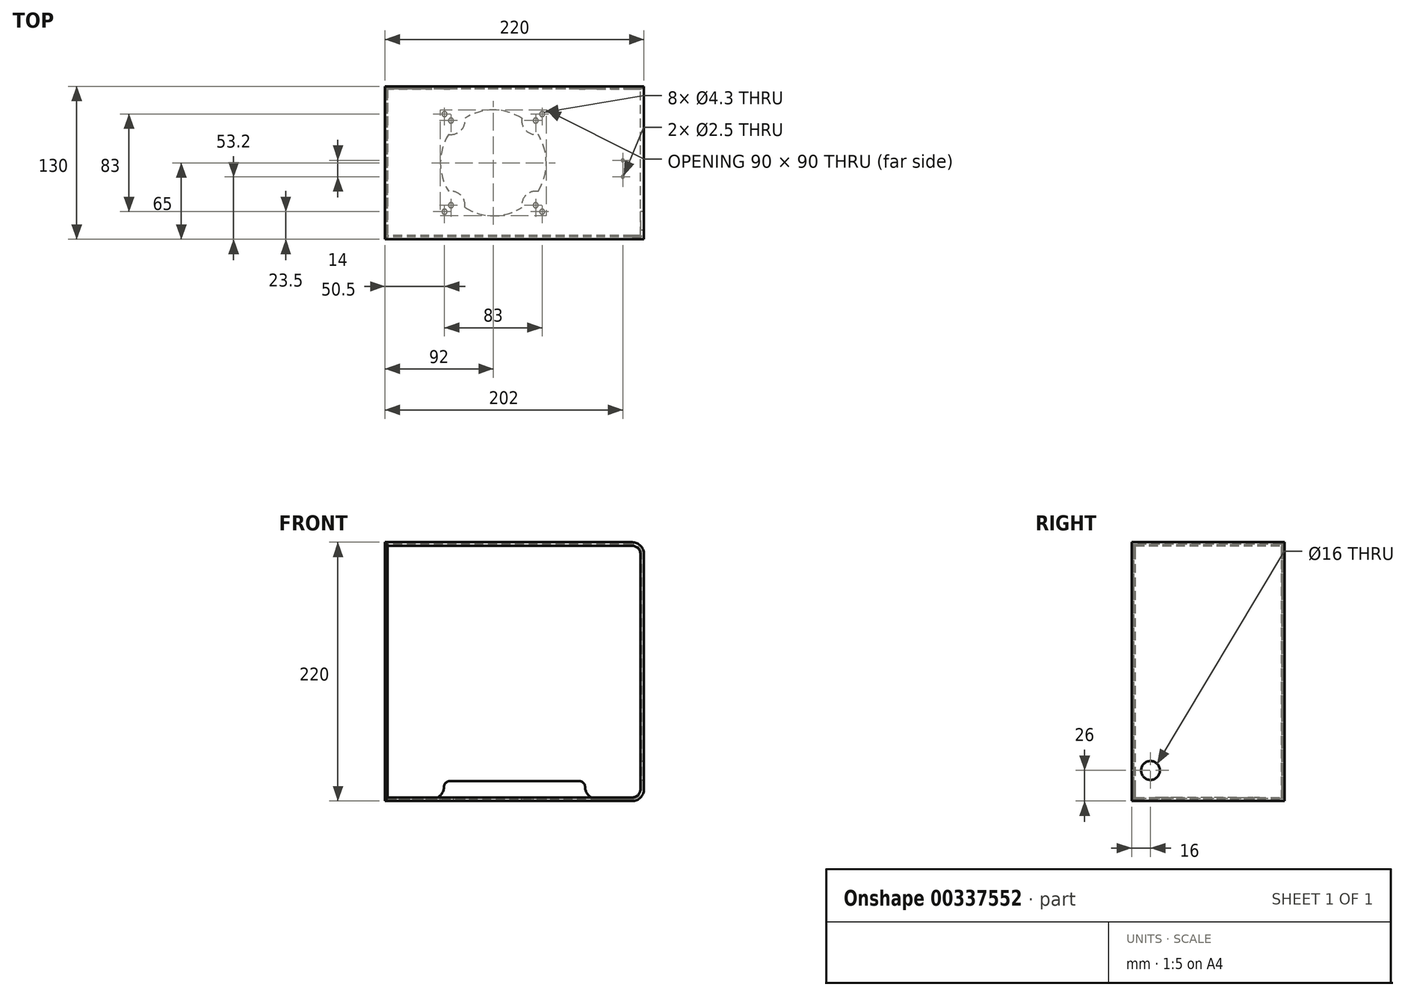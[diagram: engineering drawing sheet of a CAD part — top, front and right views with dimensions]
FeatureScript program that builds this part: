
annotation { "Feature Type Name" : "Feature", "Feature Type Description" : "" }
export const myFeature = defineFeature(function(context is Context, id is Id, definition is map)
    precondition{}
    {
        {
            var Q0;
            Q0=qCreatedBy(makeId("Right.planeOp"),FACE);
            var sketch = newSketch(context, id + "F0", { "sketchPlane" : qUnion([Q0])});
            skLineSegment(sketch, "E0.bottom", {"start": v(-65, 0) * mm, "end": v(65, 0) * mm});
            skLineSegment(sketch, "E0.top", {"start": v(-65, 3) * mm, "end": v(-63, 3) * mm});
            skLineSegment(sketch, "E0.left", {"start": v(-65, 0) * mm, "end": v(-65, 3) * mm});
            skLineSegment(sketch, "E0.right", {"start": v(65, 0) * mm, "end": v(65, 3) * mm});
            skLineSegment(sketch, "E1.top", {"start": v(-63, 1.9) * mm, "end": v(-61.8, 1.9) * mm});
            skLineSegment(sketch, "E1.left", {"start": v(-63, 3) * mm, "end": v(-63, 1.9) * mm});
            skLineSegment(sketch, "E1.right", {"start": v(-61.8, 3) * mm, "end": v(-61.8, 1.9) * mm});
            skLineSegment(sketch, "E2.trimOffspring", {"start": v(-61.8, 3) * mm, "end": v(62.8, 3) * mm});
            skLineSegment(sketch, "E3.top", {"start": v(64, 1.9) * mm, "end": v(62.8, 1.9) * mm});
            skLineSegment(sketch, "E3.left", {"start": v(64, 3) * mm, "end": v(64, 1.9) * mm});
            skLineSegment(sketch, "E3.right", {"start": v(62.8, 3) * mm, "end": v(62.8, 1.9) * mm});
            skLineSegment(sketch, "E4.trimOffspring", {"start": v(64, 3) * mm, "end": v(65, 3) * mm});
            skSolve(sketch);
        }
        {
            var Q0;
            Q0=qCreatedBy(makeId("Front.planeOp"),FACE);
            var sketch = newSketch(context, id + "F1", { "sketchPlane" : qUnion([Q0])});
            skLineSegment(sketch, "E5", {"start": v(0, 0) * mm, "end": v(210, 0) * mm});
            skLineSegment(sketch, "E6", {"start": v(220, 10) * mm, "end": v(220, 210) * mm});
            skLineSegment(sketch, "E7", {"start": v(210, 220) * mm, "end": v(0, 220) * mm});
            skPoint(sketch, "E8.visualSharp", {"position": v(220, 220) * mm});
            skArc(sketch, "E8.filletArc", {"start": v(220, 210) * mm, "mid": v(217.07, 217.07) * mm, "end": v(210, 220) * mm});
            skPoint(sketch, "E9.visualSharp", {"position": v(220, 0) * mm});
            skArc(sketch, "E9.filletArc", {"start": v(210, 0) * mm, "mid": v(217.07, 2.93) * mm, "end": v(220, 10) * mm});
            skSolve(sketch);
        }
        {
            var Q0;
            Q0=makeQuery(id+"F0.imprint","IMPRINT",FACE,{"disambiguationData":[TD([[makeQuery(id+"F0.imprint","IMPRINT",EDGE,{"derivedFrom":sQuery(id+"F0.wireOp",EDGE,"E0.bottom")}),1.0]])]});
            var Q1;
            Q1=qConstructionFilter(qBodyType(qCreatedBy(id+"F1",EDGE),BodyType.WIRE),ConstructionObject.NO);
            sweep(context, id + "F2", {"profiles" : qUnion([Q0]), "path" : qUnion([Q1])});
        }
        {
            var Q0;
            Q0=makeQuery(id+"F2.opSweep","SWEPT_FACE",FACE,{"disambiguationData":[OSD([sQuery(id+"F0.wireOp",EDGE,"E2.trimOffspring"),sQuery(id+"F1.wireOp",EDGE,"E5")])]});
            var sketch = newSketch(context, id + "F3", { "sketchPlane" : qUnion([Q0])});
            skLineSegment(sketch, "E10.bottom", {"start": v(56, 36) * mm, "end": v(128, 36) * mm, "construction": true});
            skLineSegment(sketch, "E10.top", {"start": v(56, -36) * mm, "end": v(128, -36) * mm, "construction": true});
            skLineSegment(sketch, "E10.left", {"start": v(56, 36) * mm, "end": v(56, -36) * mm, "construction": true});
            skLineSegment(sketch, "E10.right", {"start": v(128, 36) * mm, "end": v(128, -36) * mm, "construction": true});
            skLineSegment(sketch, "E11.bottom", {"start": v(50.5, 41.5) * mm, "end": v(133.5, 41.5) * mm, "construction": true});
            skLineSegment(sketch, "E11.top", {"start": v(50.5, -41.5) * mm, "end": v(133.5, -41.5) * mm, "construction": true});
            skLineSegment(sketch, "E11.left", {"start": v(50.5, 41.5) * mm, "end": v(50.5, -41.5) * mm, "construction": true});
            skLineSegment(sketch, "E11.right", {"start": v(133.5, 41.5) * mm, "end": v(133.5, -41.5) * mm, "construction": true});
            skLineSegment(sketch, "E12", {"start": v(50.5, 41.5) * mm, "end": v(56, 36) * mm, "construction": true});
            skLineSegment(sketch, "E13", {"start": v(128, -36) * mm, "end": v(133.5, -41.5) * mm, "construction": true});
            skArc(sketch, "E14", {"start": v(54.09, 24.24) * mm, "mid": v(47.72, -8.02) * mm, "end": v(65, -36) * mm});
            skLineSegment(sketch, "E15", {"start": v(56, 36) * mm, "end": v(92, 0) * mm, "construction": true});
            skLineSegment(sketch, "E16", {"start": v(92, 0) * mm, "end": v(128, -36) * mm, "construction": true});
            skCircle(sketch, "E17", {"center": v(56, 36) * mm, "radius": 2.15 * mm});
            skCircle(sketch, "E18", {"center": v(50.5, 41.5) * mm, "radius": 2.15 * mm});
            skCircle(sketch, "E19", {"center": v(56, -36) * mm, "radius": 2.15 * mm});
            skCircle(sketch, "E20", {"center": v(50.5, -41.5) * mm, "radius": 2.15 * mm});
            skCircle(sketch, "E21", {"center": v(128, 36) * mm, "radius": 2.15 * mm});
            skCircle(sketch, "E22", {"center": v(133.5, 41.5) * mm, "radius": 2.15 * mm});
            skCircle(sketch, "E23", {"center": v(133.5, -41.5) * mm, "radius": 2.15 * mm});
            skCircle(sketch, "E24", {"center": v(128, -36) * mm, "radius": 2.15 * mm});
            skCircle(sketch, "E25", {"center": v(92, 0) * mm, "radius": 39 * mm, "construction": true});
            skArc(sketch, "E26", {"start": v(54.09, 24.24) * mm, "mid": v(64.42, 27.58) * mm, "end": v(67.76, 37.91) * mm});
            skArc(sketch, "E27", {"start": v(66.57, -41.5) * mm, "mid": v(64.42, -27.58) * mm, "end": v(50.5, -25.43) * mm});
            skArc(sketch, "E28.trimOffspring", {"start": v(67.76, -37.91) * mm, "mid": v(100.02, -44.28) * mm, "end": v(128, -27) * mm});
            skArc(sketch, "E29", {"start": v(129.91, -24.24) * mm, "mid": v(124.25, -47.3) * mm, "end": v(133.5, -25.43) * mm});
            skArc(sketch, "E30", {"start": v(116.24, 37.91) * mm, "mid": v(139.3, 32.25) * mm, "end": v(117.43, 41.5) * mm});
            skArc(sketch, "E31.trimOffspring", {"start": v(116.24, 37.91) * mm, "mid": v(83.98, 44.28) * mm, "end": v(56, 27) * mm});
            skArc(sketch, "E32.trimOffspring", {"start": v(129.91, -24.24) * mm, "mid": v(136.28, 8.02) * mm, "end": v(119, 36) * mm});
            skSolve(sketch);
        }
        {
            var Q0;
            Q0=qSketchRegion(id+"F3",true);
            extrude(context, id + "F4", {"entities" : qUnion([Q0]), "operationType" : NewBodyOperationType.REMOVE, "oppositeDirection" : true, "depth" : 25 * mm});
        }
        {
            var Q0;
            Q0=makeQuery(id+"F2.opSweep","SWEPT_FACE",FACE,{"disambiguationData":[OSD([sQuery(id+"F0.wireOp",EDGE,"E0.right"),sQuery(id+"F1.wireOp",EDGE,"E5")])]});
            var sketch = newSketch(context, id + "F5", { "sketchPlane" : qUnion([Q0])});
            skLineSegment(sketch, "E33.bottom", {"start": v(-2.2, 3) * mm, "end": v(-1, 3) * mm});
            skLineSegment(sketch, "E33.top", {"start": v(-2.2, 1.9) * mm, "end": v(-1, 1.9) * mm});
            skLineSegment(sketch, "E33.left", {"start": v(-2.2, 3) * mm, "end": v(-2.2, 1.9) * mm});
            skLineSegment(sketch, "E33.right", {"start": v(-1, 3) * mm, "end": v(-1, 1.9) * mm});
            skLineSegment(sketch, "E34.bottom", {"start": v(-1, 217) * mm, "end": v(-2.2, 217) * mm});
            skLineSegment(sketch, "E34.top", {"start": v(-1, 218.1) * mm, "end": v(-2.2, 218.1) * mm});
            skLineSegment(sketch, "E34.left", {"start": v(-1, 217) * mm, "end": v(-1, 218.1) * mm});
            skLineSegment(sketch, "E34.right", {"start": v(-2.2, 217) * mm, "end": v(-2.2, 218.1) * mm});
            skSolve(sketch);
        }
        {
            var Q0;
            Q0 = qSketchRegion(id + "F5", true);
            extrude(context, id + "F6", {"entities" : qUnion([Q0]), "operationType" : NewBodyOperationType.REMOVE, "endBound" : BoundingType.THROUGH_ALL, "oppositeDirection" : true, "depth" : 25 * mm});
        }
        {
            var Q0;
            {var subQ0=sQuery(id+"F1.wireOp",EDGE,"E5");var subQ1=sQuery(id+"F0.wireOp",EDGE,"E2.trimOffspring");Q0=makeQuery(id+"F6.boolean.opBoolean","SPLIT",FACE,{"disambiguationData":[TD([makeQuery(id+"F4.boolean.opBoolean","COPY",FACE,{"derivedFrom":makeQuery(id+"F4.opExtrude","SWEPT_FACE",FACE,{"disambiguationData":[OSD([sQuery(id+"F3.wireOp",EDGE,"E14")])]})})])],"derivedFrom":makeQuery(id+"F2.opSweep","SWEPT_FACE",FACE,{"disambiguationData":[OSD([subQ1,subQ0])]})});}
            var sketch = newSketch(context, id + "F7", { "sketchPlane" : qUnion([Q0])});
            skCircle(sketch, "E35", {"center": v(202, 2.2) * mm, "radius": 1.5 * mm});
            skCircle(sketch, "E36", {"center": v(202, -11.8) * mm, "radius": 1.5 * mm});
            skLineSegment(sketch, "E37", {"start": v(202, -11.8) * mm, "end": v(202, 2.2) * mm, "construction": true});
            skPoint(sketch, "E38.0", {"position": v(210, 65) * mm});
            skPoint(sketch, "E39.0", {"position": v(210, -61.8) * mm});
            skSolve(sketch);
        }
        {
            var Q0;
            Q0=sQuery(id+"F7.wireOp",VERTEX,"E37.end");
            var Q1;
            Q1=sQuery(id+"F7.wireOp",VERTEX,"E37.start");
            var Q2;
            Q2=makeQuery(id+"F2.opSweep","SWEPT_BODY",BODY,{"disambiguationData":[OSD([sQuery(id+"F0.wireOp",EDGE,"E0.bottom"),sQuery(id+"F0.wireOp",EDGE,"E0.top"),sQuery(id+"F0.wireOp",EDGE,"E0.left"),sQuery(id+"F0.wireOp",EDGE,"E0.right"),sQuery(id+"F0.wireOp",EDGE,"E1.top"),sQuery(id+"F0.wireOp",EDGE,"E1.left"),sQuery(id+"F0.wireOp",EDGE,"E1.right"),sQuery(id+"F0.wireOp",EDGE,"E2.trimOffspring"),sQuery(id+"F1.wireOp",EDGE,"E7")])]});
            hole(context, id + "F8", {"style" : HoleStyle.SIMPLE, "endStyle" : HoleEndStyle.THROUGH, "standardTappedOrClearance" : lookupTablePath({ "standard" : "ISO", "engagement" : "75%", "pitch" : "0.5 mm", "size" : "M3", "type" : "Tapped" }), "standardBlindInLast" : lookupTablePath({ "standard" : "ISO", "engagement" : "75%", "pitch" : "0.5 mm", "size" : "M3", "type" : "Tapped" }), "holeDiameter" : 2.5 * mm, "showTappedDepth" : true, "isTappedThrough" : true, "tappedDepth" : 12 * mm, "tapClearance" : 3, "locations" : qUnion([Q0, Q1]), "scope" : qUnion([Q2]), "majorDiameter" : 3 * mm});
        }
        {
            var Q0;
            Q0=makeQuery(id+"F2.opSweep","SWEPT_FACE",FACE,{"disambiguationData":[OSD([sQuery(id+"F0.wireOp",EDGE,"E0.bottom"),sQuery(id+"F1.wireOp",EDGE,"E6")])]});
            var sketch = newSketch(context, id + "F9", { "sketchPlane" : qUnion([Q0])});
            skCircle(sketch, "E40", {"center": v(-49, 26) * mm, "radius": 8 * mm});
            skSolve(sketch);
        }
        {
            var Q0;
            Q0 = qSketchRegion(id + "F9", true);
            extrude(context, id + "F10", {"entities" : qUnion([Q0]), "operationType" : NewBodyOperationType.REMOVE, "endBound" : BoundingType.UP_TO_NEXT, "oppositeDirection" : true, "depth" : 25 * mm});
        }
        {
            var Q0;
            Q0=makeQuery(id+"F6.boolean.opBoolean","COPY",FACE,{"derivedFrom":makeQuery(id+"F6.opExtrude","SWEPT_FACE",FACE,{"disambiguationData":[OSD([sQuery(id+"F5.wireOp",EDGE,"E33.right")])]})});
            var sketch = newSketch(context, id + "F11", { "sketchPlane" : qUnion([Q0])});
            skLineSegment(sketch, "E41.bottom", {"start": v(62.5, 1.9) * mm, "end": v(-63, 1.9) * mm});
            skLineSegment(sketch, "E41.top", {"start": v(62.5, 218.1) * mm, "end": v(-63, 218.1) * mm});
            skLineSegment(sketch, "E41.left", {"start": v(62.5, 1.9) * mm, "end": v(62.5, 218.1) * mm});
            skLineSegment(sketch, "E41.right", {"start": v(-63, 1.9) * mm, "end": v(-63, 218.1) * mm});
            skPoint(sketch, "E42.0", {"position": v(62.5, 218.1) * mm});
            skPoint(sketch, "E43.0", {"position": v(-63, 218.1) * mm});
            skSolve(sketch);
        }
        {
            var Q0;
            Q0 = qSketchRegion(id + "F11", true);
            extrude(context, id + "F12", {"entities" : qUnion([Q0]), "depth" : 1 * mm});
        }
        {
            var Q0;
            {var subQ2=sQuery(id+"F1.wireOp",EDGE,"E5");Q0=makeQuery(id+"F6.boolean.opBoolean","SPLIT",FACE,{"disambiguationData":[TD([makeQuery(id+"F6.opExtrude","SWEPT_FACE",FACE,{"disambiguationData":[OSD([sQuery(id+"F5.wireOp",EDGE,"E33.left")])]})])],"derivedFrom":makeQuery(id+"F2.opSweep","SWEPT_FACE",FACE,{"disambiguationData":[OSD([sQuery(id+"F0.wireOp",EDGE,"E3.right"),subQ2])]})});}
            var sketch = newSketch(context, id + "F13", { "sketchPlane" : qUnion([Q0])});
            skPoint(sketch, "E44.0", {"position": v(0, 1.9) * mm});
            skLineSegment(sketch, "E45.bottom", {"start": v(0, 1.9) * mm, "end": v(-40, 1.9) * mm});
            skLineSegment(sketch, "E45.top", {"start": v(0, 218.1) * mm, "end": v(-210, 218.1) * mm});
            skLineSegment(sketch, "E45.left", {"start": v(0, 1.9) * mm, "end": v(0, 218.1) * mm});
            skArc(sketch, "E46", {"start": v(-210, 1.9) * mm, "mid": v(-215.73, 4.27) * mm, "end": v(-218.1, 10) * mm});
            skLineSegment(sketch, "E47", {"start": v(-218.1, 10) * mm, "end": v(-218.1, 210) * mm});
            skArc(sketch, "E48", {"start": v(-218.1, 210) * mm, "mid": v(-215.73, 215.73) * mm, "end": v(-210, 218.1) * mm});
            skLineSegment(sketch, "E49", {"start": v(-180, 190.27) * mm, "end": v(-180, 1.9) * mm, "construction": true});
            skLineSegment(sketch, "E50", {"start": v(-40, 1.9) * mm, "end": v(-40, 151.3) * mm, "construction": true});
            skLineSegment(sketch, "E51.trimOffspring", {"start": v(-180, 1.9) * mm, "end": v(-210, 1.9) * mm});
            skLineSegment(sketch, "E52", {"start": v(-165, 16.9) * mm, "end": v(-55, 16.9) * mm});
            skArc(sketch, "E53", {"start": v(-180, 1.9) * mm, "mid": v(-172.93, 4.83) * mm, "end": v(-170, 11.9) * mm});
            skArc(sketch, "E54", {"start": v(-170, 11.9) * mm, "mid": v(-168.54, 15.44) * mm, "end": v(-165, 16.9) * mm});
            skArc(sketch, "E55", {"start": v(-40, 1.9) * mm, "mid": v(-47.07, 4.83) * mm, "end": v(-50, 11.9) * mm});
            skArc(sketch, "E56", {"start": v(-50, 11.9) * mm, "mid": v(-51.46, 15.44) * mm, "end": v(-55, 16.9) * mm});
            skLineSegment(sketch, "E57", {"start": v(-180, 11.9) * mm, "end": v(-165, 11.9) * mm, "construction": true});
            skLineSegment(sketch, "E58", {"start": v(-55, 11.9) * mm, "end": v(-40, 11.9) * mm, "construction": true});
            skLineSegment(sketch, "E59", {"start": v(-165, 11.9) * mm, "end": v(-165, 16.9) * mm, "construction": true});
            skLineSegment(sketch, "E60", {"start": v(-55, 11.9) * mm, "end": v(-55, 16.9) * mm, "construction": true});
            skLineSegment(sketch, "E61", {"start": v(-165, 11.9) * mm, "end": v(-55, 11.9) * mm, "construction": true});
            skSolve(sketch);
        }
        {
            var Q0;
            Q0 = qSketchRegion(id + "F13", true);
            extrude(context, id + "F14", {"entities" : qUnion([Q0]), "depth" : 1 * mm});
        }
    });
